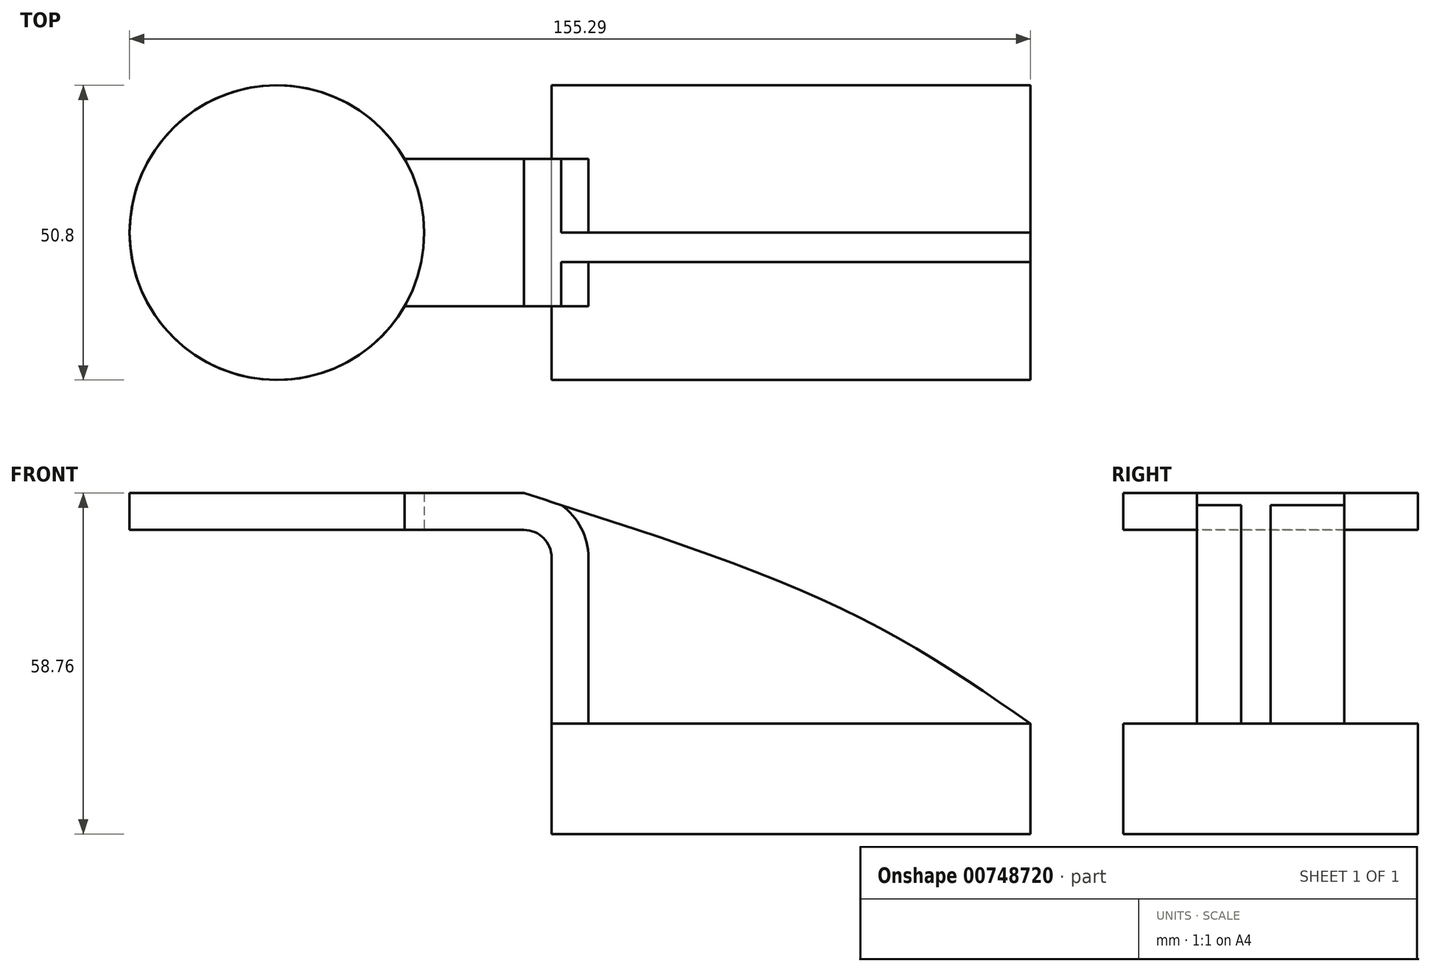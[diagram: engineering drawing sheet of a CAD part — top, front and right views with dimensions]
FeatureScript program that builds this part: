
annotation { "Feature Type Name" : "Feature", "Feature Type Description" : "" }
export const myFeature = defineFeature(function(context is Context, id is Id, definition is map)
    precondition{}
    {
        {
            var Q0;
            Q0=qCreatedBy(makeId("Front.planeOp"),FACE);
            var sketch = newSketch(context, id + "F0", { "sketchPlane" : qUnion([Q0])});
            skLineSegment(sketch, "E0.bottom", {"start": v(41.28, 9.52) * mm, "end": v(-41.27, 9.52) * mm});
            skLineSegment(sketch, "E0.top", {"start": v(41.28, -9.53) * mm, "end": v(-41.27, -9.53) * mm});
            skLineSegment(sketch, "E0.left", {"start": v(41.28, 9.52) * mm, "end": v(41.28, -9.53) * mm});
            skLineSegment(sketch, "E0.right", {"start": v(-41.27, 9.52) * mm, "end": v(-41.27, -9.52) * mm});
            skPoint(sketch, "E0.middle", {"position": v(0, 0) * mm});
            skLineSegment(sketch, "E1.bottom", {"start": v(-114.01, 38.1) * mm, "end": v(-63.21, 38.1) * mm});
            skLineSegment(sketch, "E1.top", {"start": v(-114.01, 66.67) * mm, "end": v(-63.21, 66.67) * mm});
            skLineSegment(sketch, "E1.left", {"start": v(-114.01, 38.1) * mm, "end": v(-114.01, 66.67) * mm});
            skLineSegment(sketch, "E1.right", {"start": v(-63.21, 38.1) * mm, "end": v(-63.21, 66.67) * mm});
            skPoint(sketch, "E1.middle", {"position": v(-88.61, 52.39) * mm});
            skLineSegment(sketch, "E2", {"start": v(-41.27, 9.53) * mm, "end": v(-41.27, 38.1) * mm});
            skArc(sketch, "E3", {"start": v(-41.27, 38.1) * mm, "mid": v(-42.67, 41.48) * mm, "end": v(-46.05, 42.88) * mm});
            skLineSegment(sketch, "E4", {"start": v(-46.05, 42.88) * mm, "end": v(-88.61, 42.88) * mm});
            skLineSegment(sketch, "E5.0", {"start": v(-46.05, 49.23) * mm, "end": v(-88.61, 49.23) * mm});
            skArc(sketch, "E5.1", {"start": v(-34.92, 38.1) * mm, "mid": v(-38.18, 45.97) * mm, "end": v(-46.05, 49.23) * mm});
            skLineSegment(sketch, "E5.2", {"start": v(-34.92, 9.53) * mm, "end": v(-34.92, 38.1) * mm});
            skLineSegment(sketch, "E6", {"start": v(-88.61, 49.23) * mm, "end": v(-88.61, 42.88) * mm});
            skFitSpline(sketch, "E7", {"points": [v(41.27, 9.52) * mm, v(9.03, 29.17) * mm, v(-46.05, 49.23) * mm], "startDerivative": vector(-66.44, 45.9) * mm, "endDerivative": vector(-106.74, 33.94) * mm});
            skLineSegment(sketch, "E8", {"start": v(-88.61, 40.39) * mm, "end": v(-88.61, 59.44) * mm});
            skSolve(sketch);
        }
        {
            var Q0;
            Q0=makeQuery(id+"F0.imprint","IMPRINT",FACE,{"disambiguationData":[TD([[makeQuery(id+"F0.imprint","IMPRINT",EDGE,{"derivedFrom":sQuery(id+"F0.wireOp",EDGE,"E0.top")}),-1.0]])]});
            extrude(context, id + "F1", {"entities" : qUnion([Q0]), "endBound" : BoundingType.SYMMETRIC, "depth" : 50.8 * mm, "offsetDistance" : 25.4 * mm});
        }
        {
            var Q0;
            {var subQ1=sQuery(id+"F0.wireOp",EDGE,"E2");Q0=makeQuery(id+"F0.imprint","IMPRINT",FACE,{"disambiguationData":[TD([[makeQuery(id+"F0.imprint","IMPRINT",EDGE,{"derivedFrom":subQ1}),-1.0]])]});}
            var Q1;
            {var subQ5=sQuery(id+"F0.wireOp",EDGE,"E6");Q1=makeQuery(id+"F0.imprint","IMPRINT",FACE,{"disambiguationData":[TD([[makeQuery(id+"F0.imprint","IMPRINT",EDGE,{"derivedFrom":subQ5}),1.0]])]});}
            extrude(context, id + "F2", {"entities" : qUnion([Q0, Q1]), "operationType" : NewBodyOperationType.ADD, "endBound" : BoundingType.SYMMETRIC, "depth" : 25.4 * mm, "offsetDistance" : 25.4 * mm});
        }
        {
            var Q0;
            {var subQ3=sQuery(id+"F0.wireOp",EDGE,"E5.2");Q0=makeQuery(id+"F0.imprint","IMPRINT",FACE,{"disambiguationData":[TD([[makeQuery(id+"F0.imprint","IMPRINT",EDGE,{"derivedFrom":subQ3}),-1.0]])]});}
            extrude(context, id + "F3", {"entities" : qUnion([Q0]), "operationType" : NewBodyOperationType.ADD, "depth" : 5.08 * mm, "offsetDistance" : 25.4 * mm});
        }
        {
            var Q0;
            {var subQ0=sQuery(id+"F0.wireOp",EDGE,"E4");var subQ1=sQuery(id+"F0.wireOp",EDGE,"E1.right");var subQ2=makeQuery(id+"F0.imprint","INTERSECT",VERTEX,{"derivedFrom":[subQ1,subQ0]});Q0=makeQuery(id+"F0.imprint","IMPRINT",FACE,{"disambiguationData":[TD([[makeQuery(id+"F0.imprint","IMPRINT",EDGE,{"disambiguationData":[TD([[subQ2,-1.0]])],"derivedFrom":subQ1}),1.0]])]});}
            var Q1;
            Q1=sQuery(id+"F0.wireOp",EDGE,"E8");
            revolve(context, id + "F4", {"surfaceOperationType" : NewSurfaceOperationType.NEW, "entities" : qUnion([Q0]), "axis" : qUnion([Q1]), "revolveType" : RevolveType.FULL});
        }
    });
